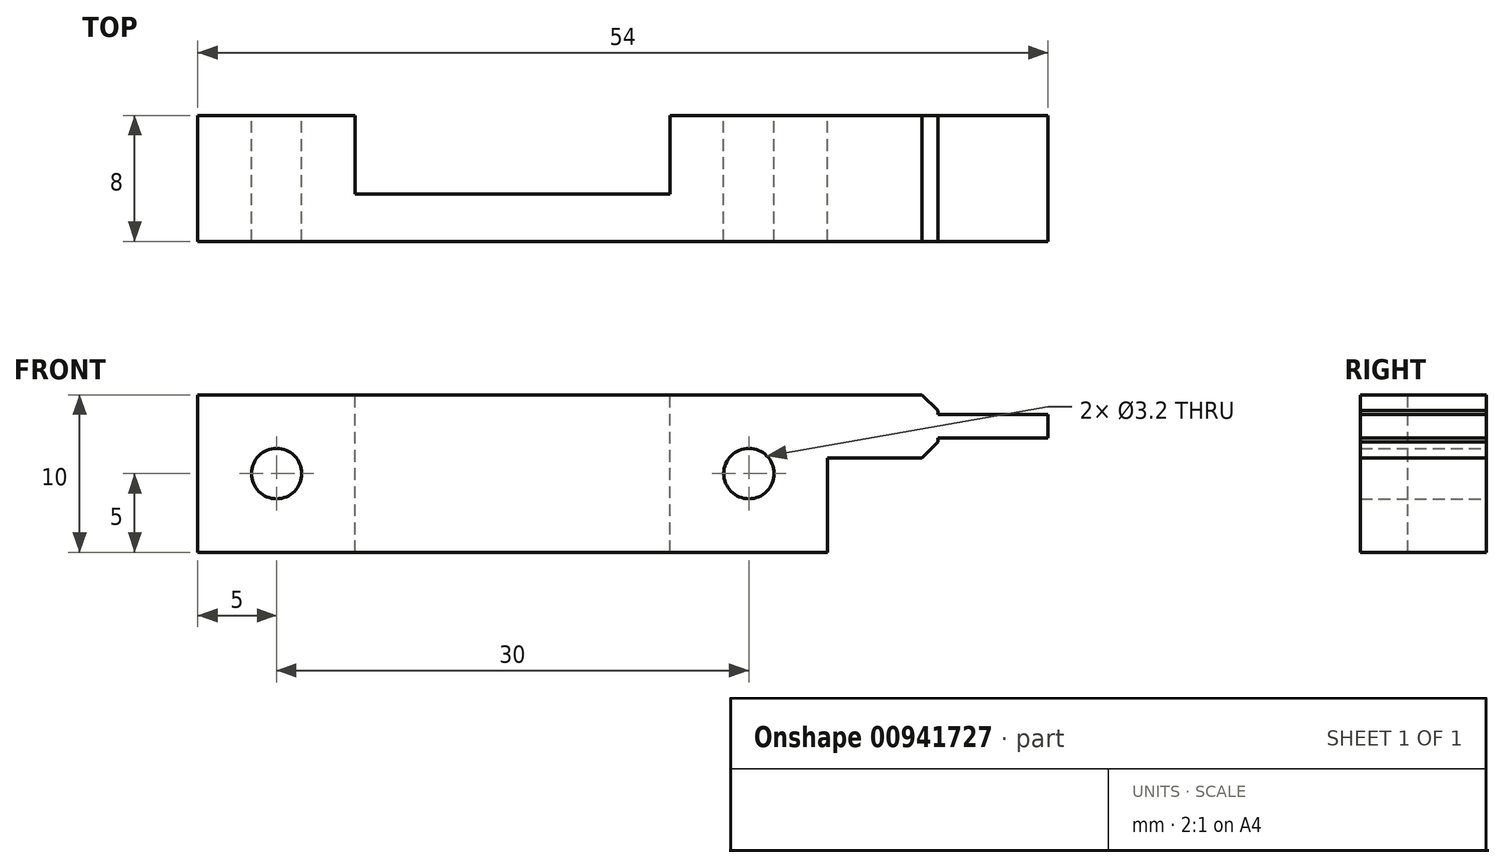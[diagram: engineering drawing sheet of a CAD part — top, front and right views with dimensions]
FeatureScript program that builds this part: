
annotation { "Feature Type Name" : "Feature", "Feature Type Description" : "" }
export const myFeature = defineFeature(function(context is Context, id is Id, definition is map)
    precondition{}
    {
        {
            var Q0;
            Q0=qCreatedBy(makeId("Front.planeOp"),FACE);
            var sketch = newSketch(context, id + "F0", { "sketchPlane" : qUnion([Q0])});
            skLineSegment(sketch, "E0.bottom", {"start": v(-20, 5) * mm, "end": v(20, 5) * mm});
            skLineSegment(sketch, "E0.top", {"start": v(-20, -5) * mm, "end": v(20, -5) * mm});
            skLineSegment(sketch, "E0.left", {"start": v(-20, 5) * mm, "end": v(-20, -5) * mm});
            skLineSegment(sketch, "E0.right", {"start": v(20, 5) * mm, "end": v(20, -5) * mm});
            skPoint(sketch, "E0.middle", {"position": v(0, 0) * mm});
            skSolve(sketch);
        }
        {
            var Q0;
            Q0 = qSketchRegion(id + "F0", true);
            extrude(context, id + "F1", {"entities" : qUnion([Q0]), "depth" : 8 * mm, "offsetDistance" : 25 * mm});
        }
        {
            var Q0;
            Q0=makeQuery(id+"F1.opExtrude","SWEPT_FACE",FACE,{"disambiguationData":[OSD([sQuery(id+"F0.wireOp",EDGE,"E0.bottom")])]});
            var sketch = newSketch(context, id + "F2", { "sketchPlane" : qUnion([Q0])});
            skLineSegment(sketch, "E1.bottom", {"start": v(-10, 5) * mm, "end": v(10, 5) * mm});
            skLineSegment(sketch, "E1.top", {"start": v(-10, -5) * mm, "end": v(10, -5) * mm});
            skLineSegment(sketch, "E1.left", {"start": v(-10, 5) * mm, "end": v(-10, -5) * mm});
            skLineSegment(sketch, "E1.right", {"start": v(10, 5) * mm, "end": v(10, -5) * mm});
            skPoint(sketch, "E1.middle", {"position": v(0, 0) * mm});
            skSolve(sketch);
        }
        {
            var Q0;
            {var subQ0=sQuery(id+"F2.wireOp",EDGE,"E1.top");Q0=makeQuery(id+"F2.imprint","IMPRINT",FACE,{"disambiguationData":[TD([[makeQuery(id+"F2.imprint","IMPRINT",EDGE,{"derivedFrom":subQ0}),1.0]])]});}
            extrude(context, id + "F3", {"entities" : qUnion([Q0]), "operationType" : NewBodyOperationType.REMOVE, "endBound" : BoundingType.UP_TO_NEXT, "oppositeDirection" : true, "depth" : 25 * mm, "offsetDistance" : 25 * mm});
        }
        {
            var Q0;
            {var subQ0=sQuery(id+"F0.wireOp",EDGE,"E0.bottom");var subQ1=sQuery(id+"F0.wireOp",EDGE,"E0.right");var subQ2=sQuery(id+"F0.wireOp",EDGE,"E0.top");Q0=makeQuery(id+"F3.boolean.opBoolean","SPLIT",FACE,{"disambiguationData":[TD([makeQuery(id+"F1.opExtrude","SWEPT_FACE",FACE,{"disambiguationData":[OSD([subQ1])]})])],"derivedFrom":makeQuery(id+"F1.opExtrude","CAP_FACE",FACE,{"disambiguationData":[OSD([subQ0,subQ2,sQuery(id+"F0.wireOp",EDGE,"E0.left"),subQ1])],"isStart":true})});}
            var sketch = newSketch(context, id + "F4", { "sketchPlane" : qUnion([Q0])});
            skCircle(sketch, "E2", {"center": v(-15, 0) * mm, "radius": 1.6 * mm});
            skPoint(sketch, "E2.centerSnap0", {"position": v(-15, 5) * mm});
            skPoint(sketch, "E2.centerSnap1", {"position": v(-20, 0) * mm});
            skSolve(sketch);
        }
        {
            var Q0;
            {var subQ0=sQuery(id+"F0.wireOp",EDGE,"E0.bottom");var subQ1=sQuery(id+"F0.wireOp",EDGE,"E0.top");var subQ2=sQuery(id+"F0.wireOp",EDGE,"E0.left");Q0=makeQuery(id+"F3.boolean.opBoolean","SPLIT",FACE,{"disambiguationData":[TD([makeQuery(id+"F1.opExtrude","SWEPT_FACE",FACE,{"disambiguationData":[OSD([subQ2])]})])],"derivedFrom":makeQuery(id+"F1.opExtrude","CAP_FACE",FACE,{"disambiguationData":[OSD([subQ0,subQ1,subQ2,sQuery(id+"F0.wireOp",EDGE,"E0.right")])],"isStart":true})});}
            var sketch = newSketch(context, id + "F5", { "sketchPlane" : qUnion([Q0])});
            skCircle(sketch, "E3", {"center": v(15, 0) * mm, "radius": 1.6 * mm});
            skPoint(sketch, "E3.centerSnap0", {"position": v(20, 0) * mm});
            skPoint(sketch, "E3.centerSnap1", {"position": v(15, 5) * mm});
            skSolve(sketch);
        }
        {
            var Q0;
            Q0=makeQuery(id+"F4.imprint","IMPRINT",FACE,{"disambiguationData":[TD([[makeQuery(id+"F4.imprint","IMPRINT",EDGE,{"derivedFrom":sQuery(id+"F4.wireOp",EDGE,"E2")}),1.0]])]});
            var Q1;
            Q1=makeQuery(id+"F5.imprint","IMPRINT",FACE,{"disambiguationData":[TD([[makeQuery(id+"F5.imprint","IMPRINT",EDGE,{"derivedFrom":sQuery(id+"F5.wireOp",EDGE,"E3")}),1.0]])]});
            extrude(context, id + "F6", {"entities" : qUnion([Q0, Q1]), "operationType" : NewBodyOperationType.REMOVE, "endBound" : BoundingType.UP_TO_NEXT, "oppositeDirection" : true, "depth" : 25 * mm, "offsetDistance" : 25 * mm});
        }
        {
            var Q0;
            Q0=makeQuery(id+"F1.opExtrude","SWEPT_FACE",FACE,{"disambiguationData":[OSD([sQuery(id+"F0.wireOp",EDGE,"E0.right")])]});
            var sketch = newSketch(context, id + "F7", { "sketchPlane" : qUnion([Q0])});
            skLineSegment(sketch, "E4.bottom", {"start": v(-8, 1) * mm, "end": v(0, 1) * mm});
            skLineSegment(sketch, "E4.top", {"start": v(-8, 5) * mm, "end": v(0, 5) * mm});
            skLineSegment(sketch, "E4.left", {"start": v(-8, 1) * mm, "end": v(-8, 5) * mm});
            skLineSegment(sketch, "E4.right", {"start": v(0, 1) * mm, "end": v(0, 5) * mm});
            skPoint(sketch, "E4.middle", {"position": v(-4, 0) * mm});
            skPoint(sketch, "E4.middle.positionSnap0", {"position": v(-4, 5) * mm});
            skPoint(sketch, "E4.centerSnap0", {"position": v(-4, 5) * mm});
            skSolve(sketch);
        }
        {
            var Q0;
            Q0=makeQuery(id+"F7.imprint","IMPRINT",FACE,{"disambiguationData":[TD([[makeQuery(id+"F7.imprint","IMPRINT",EDGE,{"derivedFrom":sQuery(id+"F7.wireOp",EDGE,"E4.bottom")}),1.0]])]});
            extrude(context, id + "F8", {"entities" : qUnion([Q0]), "operationType" : NewBodyOperationType.ADD, "depth" : 7 * mm, "offsetDistance" : 25 * mm});
        }
        {
            var Q0;
            Q0=makeQuery(id+"F8.opExtrude","CAP_FACE",FACE,{"disambiguationData":[OSD([sQuery(id+"F7.wireOp",EDGE,"E4.bottom"),sQuery(id+"F7.wireOp",EDGE,"E4.top"),sQuery(id+"F7.wireOp",EDGE,"E4.left"),sQuery(id+"F7.wireOp",EDGE,"E4.right")])],"isStart":false});
            var sketch = newSketch(context, id + "F9", { "sketchPlane" : qUnion([Q0])});
            skLineSegment(sketch, "E5.bottom", {"start": v(0, 2.25) * mm, "end": v(-8, 2.25) * mm});
            skLineSegment(sketch, "E5.top", {"start": v(0, 3.75) * mm, "end": v(-8, 3.75) * mm});
            skLineSegment(sketch, "E5.left", {"start": v(0, 2.25) * mm, "end": v(0, 3.75) * mm});
            skLineSegment(sketch, "E5.right", {"start": v(-8, 2.25) * mm, "end": v(-8, 3.75) * mm});
            skPoint(sketch, "E5.middle", {"position": v(-4, 3) * mm});
            skPoint(sketch, "E5.middle.positionSnap0", {"position": v(-4, 1) * mm});
            skPoint(sketch, "E5.middle.positionSnap1", {"position": v(-8, 3) * mm});
            skPoint(sketch, "E5.centerSnap0", {"position": v(-4, 1) * mm});
            skPoint(sketch, "E5.centerSnap1", {"position": v(-8, 3) * mm});
            skSolve(sketch);
        }
        {
            var Q0;
            Q0 = qSketchRegion(id + "F9", true);
            extrude(context, id + "F10", {"entities" : qUnion([Q0]), "operationType" : NewBodyOperationType.ADD, "depth" : 7 * mm, "offsetDistance" : 25 * mm});
        }
        {
            var Q0;
            Q0=makeQuery(id+"F8.opExtrude","CAP_EDGE",EDGE,{"disambiguationData":[OSD([sQuery(id+"F7.wireOp",EDGE,"E4.bottom")])],"isStart":false});
            var Q1;
            Q1=makeQuery(id+"F8.opExtrude","CAP_EDGE",EDGE,{"disambiguationData":[OSD([sQuery(id+"F7.wireOp",EDGE,"E4.top")])],"isStart":false});
            chamfer(context, id + "F11", {"entities" : qUnion([Q0, Q1]), "width" : 1 * mm, "tangentPropagation" : true});
        }
    });
